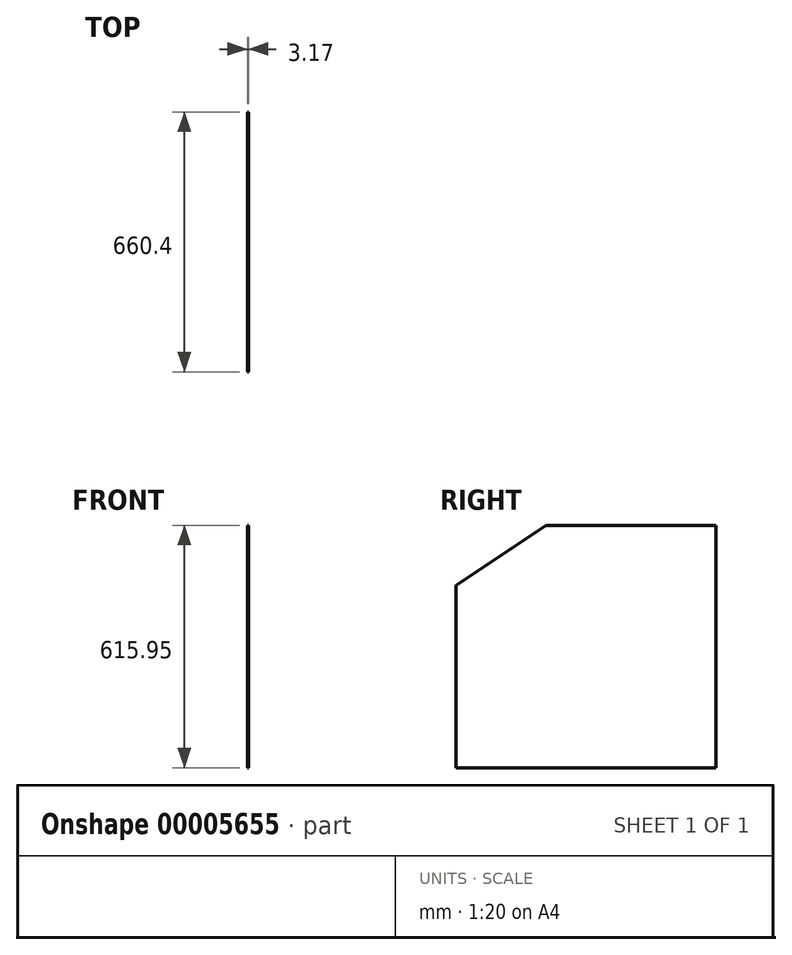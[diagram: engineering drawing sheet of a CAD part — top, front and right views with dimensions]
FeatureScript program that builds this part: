
annotation { "Feature Type Name" : "Feature", "Feature Type Description" : "" }
export const myFeature = defineFeature(function(context is Context, id is Id, definition is map)
    precondition{}
    {
        {
            var Q0;
            Q0=qCreatedBy(makeId("Right.planeOp"),FACE);
            var sketch = newSketch(context, id + "F0", { "sketchPlane" : qUnion([Q0])});
            skLineSegment(sketch, "E0.bottom", {"start": v(0, 0) * mm, "end": v(-431.8, 0) * mm});
            skLineSegment(sketch, "E0.top", {"start": v(0, 615.95) * mm, "end": v(-431.8, 615.95) * mm});
            skLineSegment(sketch, "E0.left", {"start": v(0, 0) * mm, "end": v(0, 615.95) * mm});
            skLineSegment(sketch, "E0.right", {"start": v(-431.8, 0) * mm, "end": v(-431.8, 615.95) * mm, "construction": true});
            skLineSegment(sketch, "E1", {"start": v(-431.8, 615.95) * mm, "end": v(-660.4, 463.55) * mm});
            skLineSegment(sketch, "E2", {"start": v(-660.4, 463.55) * mm, "end": v(-431.8, 463.55) * mm, "construction": true});
            skLineSegment(sketch, "E3", {"start": v(-660.4, 463.55) * mm, "end": v(-660.4, 0) * mm});
            skLineSegment(sketch, "E4", {"start": v(-431.8, 0) * mm, "end": v(-660.4, 0) * mm});
            skSolve(sketch);
        }
        {
            var Q0;
            Q0 = qSketchRegion(id + "F0", true);
            extrude(context, id + "F1", {"entities" : qUnion([Q0]), "depth" : 3.17 * mm});
        }
    });
